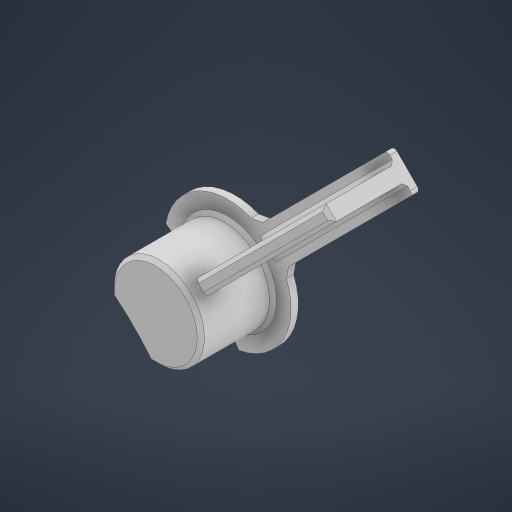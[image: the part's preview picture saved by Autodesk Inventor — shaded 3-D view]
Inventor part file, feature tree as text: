
AUTODESK INVENTOR PART (.ipt)
format: ipt  version: 2023.1 (Build 271208000, 208)  size: 555,008 bytes
history: native  units: mm
features: extrude x2, chamfer x2, sketch x2
ambient origin geometry x8: Origin, YZ Plane, XZ Plane, XY Plane, X Axis, Y Axis, Z Axis, Center Point
bodies: Body1 (feature_tree)
feature tree (6):
  extrude  "Extrusion2"  TaperAngle=45.0deg  [1 undecoded]
  extrude  "Extrusion3"  Depth=35.0mm
  chamfer  "Chamfer6"  Distance=142.0mm
  chamfer  "Chamfer7"  Angle=112.5deg  [1 undecoded]
  sketch  "Sketch3"  dims[d26=147.0mm d27=45.0deg]
  sketch  "Sketch4"  dims[d28=159.154943mm d29=35.0mm d30=142.0mm d31=112.5deg d32=157.5deg d33=5.0mm d34=5.0mm d35=1.0mm d36=2.0mm d37=0.0mm d38=25.0mm d39=2.0mm d40=2.0mm d41=5.0mm d42=20.0mm d43=0.0mm d56=3.0mm d60=1.0mm d61=2.0mm d62=45.0deg d63=2.0mm d64=2.0mm d65=45.0deg d66=187.154943mm d67=35.0mm]
note: 2 required parameter values undecoded (feature->parameter linkage not recoverable at this tier; creation-order binding heuristic only, values carry confidence <= 0.55)
